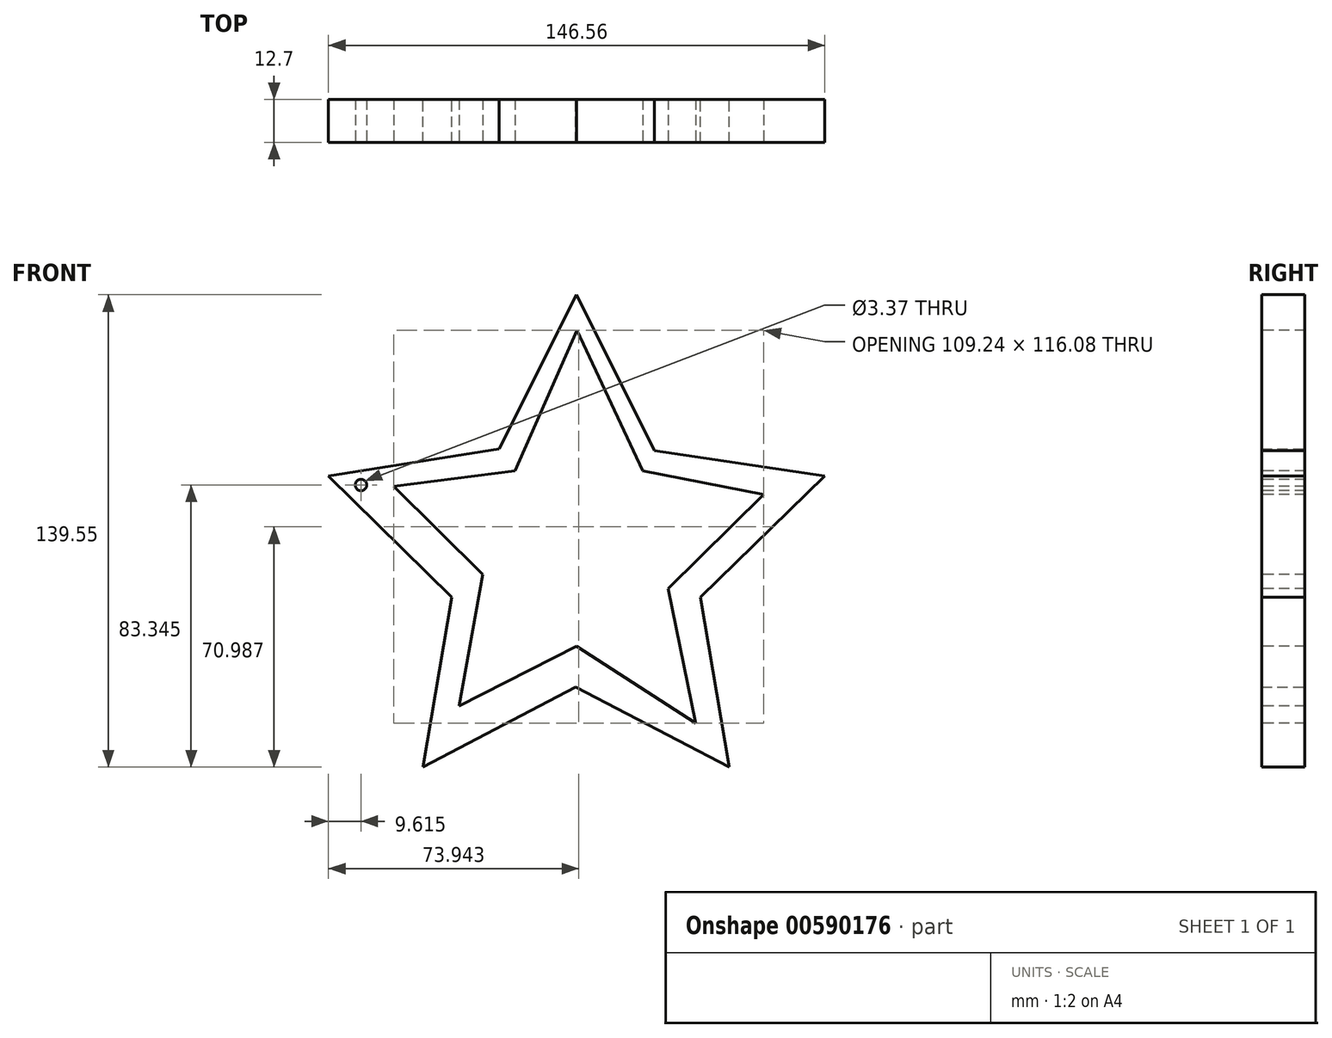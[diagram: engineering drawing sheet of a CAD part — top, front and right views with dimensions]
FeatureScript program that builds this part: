
annotation { "Feature Type Name" : "Feature", "Feature Type Description" : "" }
export const myFeature = defineFeature(function(context is Context, id is Id, definition is map)
    precondition{}
    {
        {
            var Q0;
            Q0=qCreatedBy(makeId("Front.planeOp"),FACE);
            var sketch = newSketch(context, id + "F0", { "sketchPlane" : qUnion([Q0])});
            skLineSegment(sketch, "E0", {"start": v(-16.38, 0) * mm, "end": v(-39.2, -45.54) * mm});
            skLineSegment(sketch, "E1", {"start": v(-39.2, -45.54) * mm, "end": v(-89.66, -53.55) * mm});
            skLineSegment(sketch, "E2", {"start": v(-89.66, -53.55) * mm, "end": v(-53.23, -89.36) * mm});
            skLineSegment(sketch, "E3", {"start": v(-53.23, -89.36) * mm, "end": v(-61.75, -139.55) * mm});
            skLineSegment(sketch, "E4", {"start": v(-61.75, -139.55) * mm, "end": v(-16.67, -115.9) * mm});
            skLineSegment(sketch, "E5", {"start": v(-16.67, -115.9) * mm, "end": v(28.66, -139.55) * mm});
            skLineSegment(sketch, "E6", {"start": v(28.66, -139.55) * mm, "end": v(20.14, -89.36) * mm});
            skLineSegment(sketch, "E7", {"start": v(20.14, -89.36) * mm, "end": v(56.9, -53.55) * mm});
            skLineSegment(sketch, "E8", {"start": v(56.9, -53.55) * mm, "end": v(6.62, -46.04) * mm});
            skLineSegment(sketch, "E9", {"start": v(6.62, -46.04) * mm, "end": v(-16.38, 0) * mm});
            skSolve(sketch);
        }
        {
            var Q0;
            Q0=qSketchRegion(id+"F0",true);
            extrude(context, id + "F1", {"entities" : qUnion([Q0]), "depth" : 12.7 * mm, "offsetDistance" : 25.4 * mm});
        }
        {
            var Q0;
            Q0=makeQuery(id+"F1.opExtrude","CAP_FACE",FACE,{"disambiguationData":[OSD([sQuery(id+"F0.wireOp",EDGE,"E0"),sQuery(id+"F0.wireOp",EDGE,"E1"),sQuery(id+"F0.wireOp",EDGE,"E2"),sQuery(id+"F0.wireOp",EDGE,"E3"),sQuery(id+"F0.wireOp",EDGE,"E4"),sQuery(id+"F0.wireOp",EDGE,"E5"),sQuery(id+"F0.wireOp",EDGE,"E6"),sQuery(id+"F0.wireOp",EDGE,"E7"),sQuery(id+"F0.wireOp",EDGE,"E8"),sQuery(id+"F0.wireOp",EDGE,"E9")])],"isStart":false});
            var sketch = newSketch(context, id + "F2", { "sketchPlane" : qUnion([Q0])});
            skLineSegment(sketch, "E10", {"start": v(-16.27, -10.52) * mm, "end": v(-34.59, -52.01) * mm});
            skLineSegment(sketch, "E11", {"start": v(-34.59, -52.01) * mm, "end": v(-70.34, -56.65) * mm});
            skLineSegment(sketch, "E12", {"start": v(-70.34, -56.65) * mm, "end": v(-44.07, -82.69) * mm});
            skLineSegment(sketch, "E13", {"start": v(-44.07, -82.69) * mm, "end": v(-51.14, -121.53) * mm});
            skLineSegment(sketch, "E14", {"start": v(-51.14, -121.53) * mm, "end": v(-16.38, -103.87) * mm});
            skLineSegment(sketch, "E15", {"start": v(-16.38, -103.87) * mm, "end": v(18.82, -126.6) * mm});
            skLineSegment(sketch, "E16", {"start": v(18.82, -126.6) * mm, "end": v(10.65, -86.88) * mm});
            skLineSegment(sketch, "E17", {"start": v(10.65, -86.88) * mm, "end": v(38.9, -59.07) * mm});
            skLineSegment(sketch, "E18", {"start": v(38.9, -59.07) * mm, "end": v(3.15, -52.01) * mm});
            skLineSegment(sketch, "E19", {"start": v(3.15, -52.01) * mm, "end": v(-16.27, -10.52) * mm});
            skSolve(sketch);
        }
        {
            var Q0;
            Q0=qSketchRegion(id+"F2",true);
            extrude(context, id + "F3", {"entities" : qUnion([Q0]), "operationType" : NewBodyOperationType.REMOVE, "oppositeDirection" : true, "depth" : 25.4 * mm, "offsetDistance" : 25.4 * mm});
        }
        {
            var Q0;
            Q0=makeQuery(id+"F1.opExtrude","CAP_FACE",FACE,{"disambiguationData":[OSD([sQuery(id+"F0.wireOp",EDGE,"E0"),sQuery(id+"F0.wireOp",EDGE,"E1"),sQuery(id+"F0.wireOp",EDGE,"E2"),sQuery(id+"F0.wireOp",EDGE,"E3"),sQuery(id+"F0.wireOp",EDGE,"E4"),sQuery(id+"F0.wireOp",EDGE,"E5"),sQuery(id+"F0.wireOp",EDGE,"E6"),sQuery(id+"F0.wireOp",EDGE,"E7"),sQuery(id+"F0.wireOp",EDGE,"E8"),sQuery(id+"F0.wireOp",EDGE,"E9")])],"isStart":false});
            var sketch = newSketch(context, id + "F4", { "sketchPlane" : qUnion([Q0])});
            skCircle(sketch, "E20", {"center": v(-80.05, -56.2) * mm, "radius": 1.69 * mm});
            skSolve(sketch);
        }
        {
            var Q0;
            Q0 = qSketchRegion(id + "F4", true);
            extrude(context, id + "F5", {"entities" : qUnion([Q0]), "operationType" : NewBodyOperationType.REMOVE, "oppositeDirection" : true, "depth" : 25.4 * mm, "offsetDistance" : 25.4 * mm});
        }
    });
